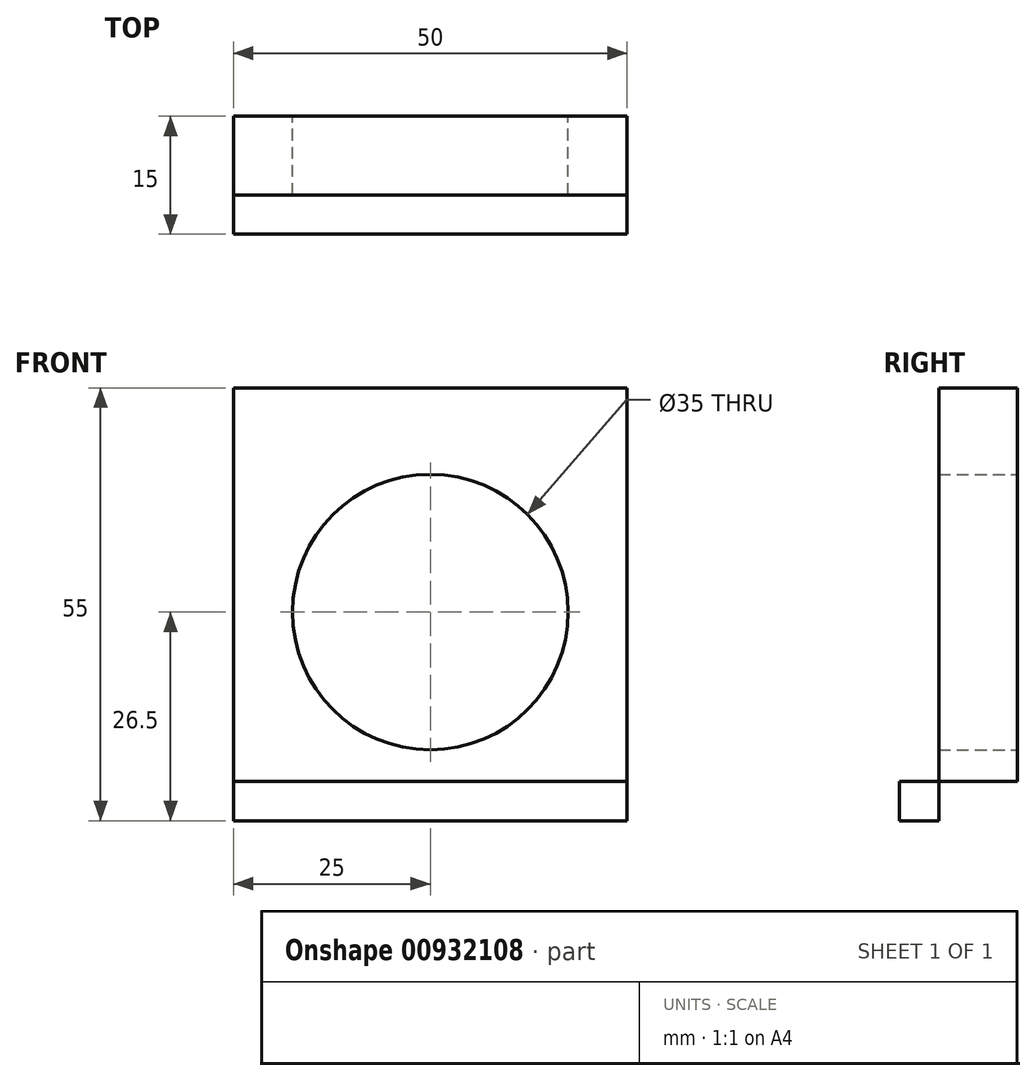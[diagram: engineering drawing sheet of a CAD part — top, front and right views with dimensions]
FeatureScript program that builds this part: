
annotation { "Feature Type Name" : "Feature", "Feature Type Description" : "" }
export const myFeature = defineFeature(function(context is Context, id is Id, definition is map)
    precondition{}
    {
        {
            var Q0;
            Q0=qCreatedBy(makeId("Front.planeOp"),FACE);
            var sketch = newSketch(context, id + "F0", { "sketchPlane" : qUnion([Q0])});
            skLineSegment(sketch, "E0.bottom", {"start": v(25, -25) * mm, "end": v(-25, -25) * mm});
            skLineSegment(sketch, "E0.top", {"start": v(25, 25) * mm, "end": v(-25, 25) * mm});
            skLineSegment(sketch, "E0.left", {"start": v(25, -25) * mm, "end": v(25, 25) * mm});
            skLineSegment(sketch, "E0.right", {"start": v(-25, -25) * mm, "end": v(-25, 25) * mm});
            skPoint(sketch, "E0.middle", {"position": v(0, 0) * mm});
            skCircle(sketch, "E1", {"center": v(0, -3.5) * mm, "radius": 17.5 * mm});
            skLineSegment(sketch, "E2.bottom", {"start": v(-25, -25) * mm, "end": v(25, -25) * mm});
            skLineSegment(sketch, "E2.top", {"start": v(-25, -30) * mm, "end": v(25, -30) * mm});
            skLineSegment(sketch, "E2.left", {"start": v(-25, -25) * mm, "end": v(-25, -30) * mm});
            skLineSegment(sketch, "E2.right", {"start": v(25, -25) * mm, "end": v(25, -30) * mm});
            skSolve(sketch);
        }
        {
            var Q0;
            Q0=makeQuery(id+"F0.imprint","IMPRINT",FACE,{"disambiguationData":[TD([[makeQuery(id+"F0.imprint","IMPRINT",EDGE,{"derivedFrom":sQuery(id+"F0.wireOp",EDGE,"E2.bottom")}),-1.0]])]});
            var Q1;
            Q1=makeQuery(id+"F0.imprint","IMPRINT",FACE,{"disambiguationData":[TD([[makeQuery(id+"F0.imprint","IMPRINT",EDGE,{"derivedFrom":sQuery(id+"F0.wireOp",EDGE,"E0.top")}),1.0]])]});
            extrude(context, id + "F1", {"entities" : qUnion([Q0, Q1]), "depth" : 10 * mm, "offsetDistance" : 25.4 * mm});
        }
        {
            var Q0;
            Q0=makeQuery(id+"F1.opExtrude","CAP_FACE",FACE,{"disambiguationData":[OSD([sQuery(id+"F0.wireOp",EDGE,"E0.top"),sQuery(id+"F0.wireOp",EDGE,"E0.left"),sQuery(id+"F0.wireOp",EDGE,"E0.right"),sQuery(id+"F0.wireOp",EDGE,"E1"),sQuery(id+"F0.wireOp",EDGE,"E2.top"),sQuery(id+"F0.wireOp",EDGE,"E2.left"),sQuery(id+"F0.wireOp",EDGE,"E2.right")])],"isStart":false});
            var sketch = newSketch(context, id + "F2", { "sketchPlane" : qUnion([Q0])});
            skLineSegment(sketch, "E3.bottom", {"start": v(-25, -30) * mm, "end": v(25, -30) * mm});
            skLineSegment(sketch, "E3.top", {"start": v(-25, -25) * mm, "end": v(25, -25) * mm});
            skLineSegment(sketch, "E3.left", {"start": v(-25, -30) * mm, "end": v(-25, -25) * mm});
            skLineSegment(sketch, "E3.right", {"start": v(25, -30) * mm, "end": v(25, -25) * mm});
            skSolve(sketch);
        }
        {
            var Q0;
            Q0 = qSketchRegion(id + "F2", true);
            extrude(context, id + "F3", {"entities" : qUnion([Q0]), "operationType" : NewBodyOperationType.ADD, "depth" : 5 * mm, "offsetDistance" : 25.4 * mm});
        }
    });
